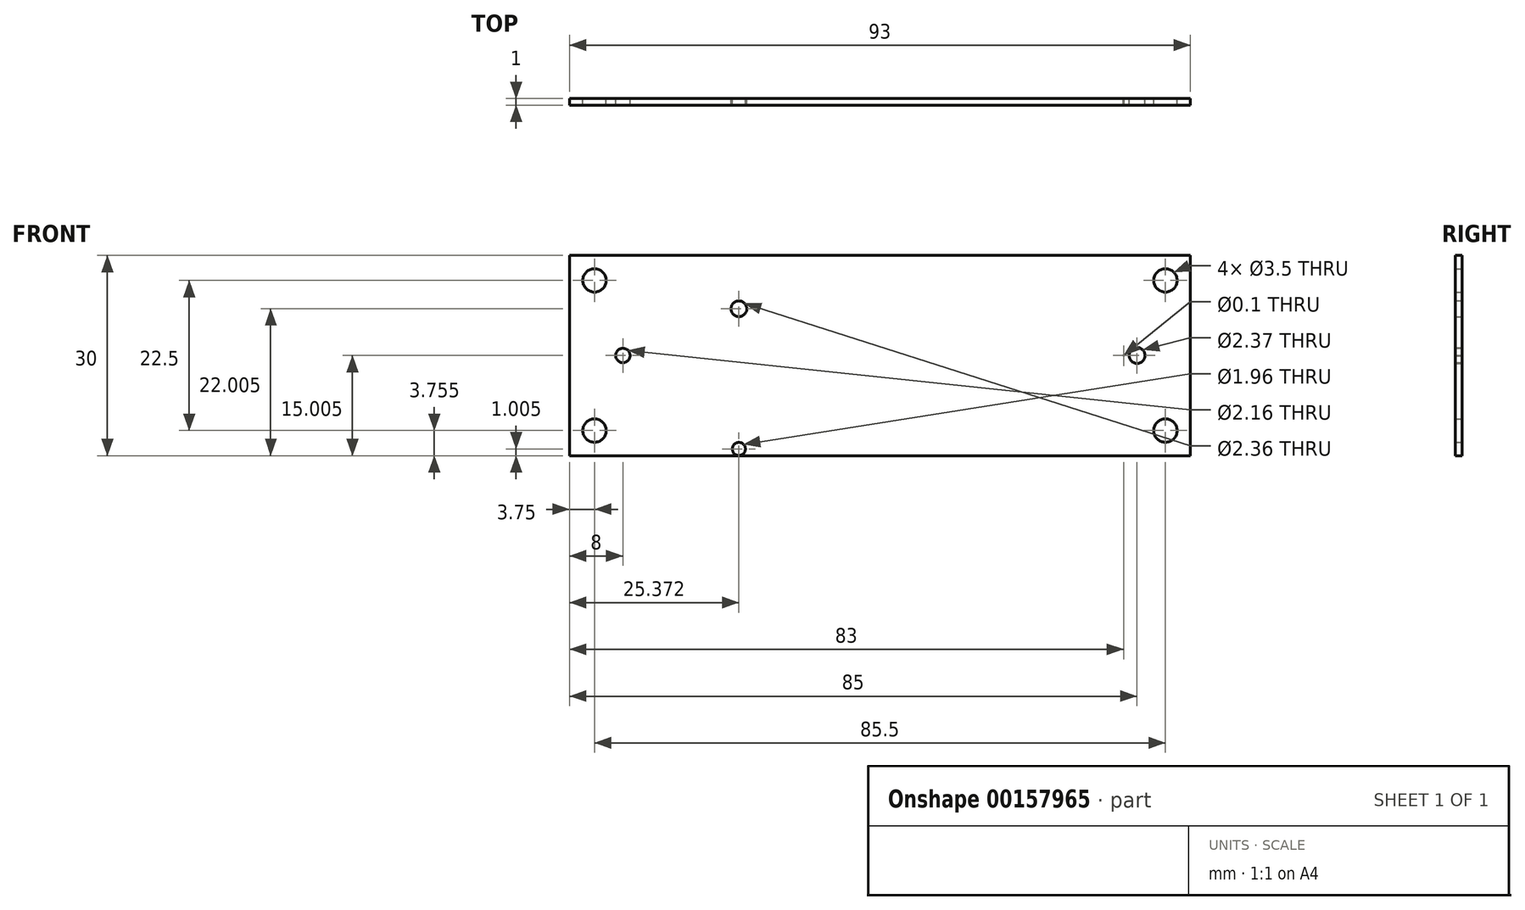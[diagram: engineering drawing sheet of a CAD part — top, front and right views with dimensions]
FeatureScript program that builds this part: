
annotation { "Feature Type Name" : "Feature", "Feature Type Description" : "" }
export const myFeature = defineFeature(function(context is Context, id is Id, definition is map)
    precondition{}
    {
        {
            var Q0;
            Q0=qCreatedBy(makeId("Front.planeOp"),FACE);
            var sketch = newSketch(context, id + "F0", { "sketchPlane" : qUnion([Q0])});
            skPoint(sketch, "E0.middle", {"position": v(0, 0) * mm});
            skLineSegment(sketch, "E1.bottom", {"start": v(-20, 12.77) * mm, "end": v(20, 12.77) * mm});
            skLineSegment(sketch, "E1.top", {"start": v(-20, -17.23) * mm, "end": v(20, -17.23) * mm});
            skLineSegment(sketch, "E1.left", {"start": v(-20, 12.77) * mm, "end": v(-20, -17.23) * mm});
            skLineSegment(sketch, "E1.right", {"start": v(20, 12.77) * mm, "end": v(20, -17.23) * mm});
            skCircle(sketch, "E2", {"center": v(-16.25, 9.02) * mm, "radius": 1.75 * mm});
            skCircle(sketch, "E3", {"center": v(69.25, 9.02) * mm, "radius": 1.75 * mm});
            skCircle(sketch, "E4", {"center": v(-16.25, -13.48) * mm, "radius": 1.75 * mm});
            skCircle(sketch, "E5", {"center": v(69.25, -13.48) * mm, "radius": 1.75 * mm});
            skLineSegment(sketch, "E6", {"start": v(-20, 0) * mm, "end": v(20, 0) * mm});
            skLineSegment(sketch, "E7", {"start": v(0, -17.23) * mm, "end": v(0, 12.77) * mm});
            skLineSegment(sketch, "E8", {"start": v(0, 12.77) * mm, "end": v(0, -17.23) * mm});
            skLineSegment(sketch, "E9.bottom", {"start": v(20, 12.77) * mm, "end": v(73, 12.77) * mm});
            skLineSegment(sketch, "E9.top", {"start": v(20, -17.23) * mm, "end": v(73, -17.23) * mm});
            skLineSegment(sketch, "E9.right", {"start": v(73, 12.77) * mm, "end": v(73, -17.23) * mm});
            skPoint(sketch, "E10.positionSnap0", {"position": v(73, -2.23) * mm});
            skCircle(sketch, "E11", {"center": v(63, -2.23) * mm, "radius": 0.05 * mm});
            skCircle(sketch, "E12", {"center": v(-12, -2.23) * mm, "radius": 1.08 * mm});
            skCircle(sketch, "E13", {"center": v(65, -2.23) * mm, "radius": 1.19 * mm});
            skCircle(sketch, "E14", {"center": v(5.37, 4.77) * mm, "radius": 1.18 * mm});
            skCircle(sketch, "E15", {"center": v(5.37, -16.23) * mm, "radius": 0.98 * mm});
            skSolve(sketch);
        }
        {
            var Q0;
            Q0=qSketchRegion(id+"F0",true);
            extrude(context, id + "F1", {"entities" : qUnion([Q0]), "depth" : 1 * mm});
        }
    });
